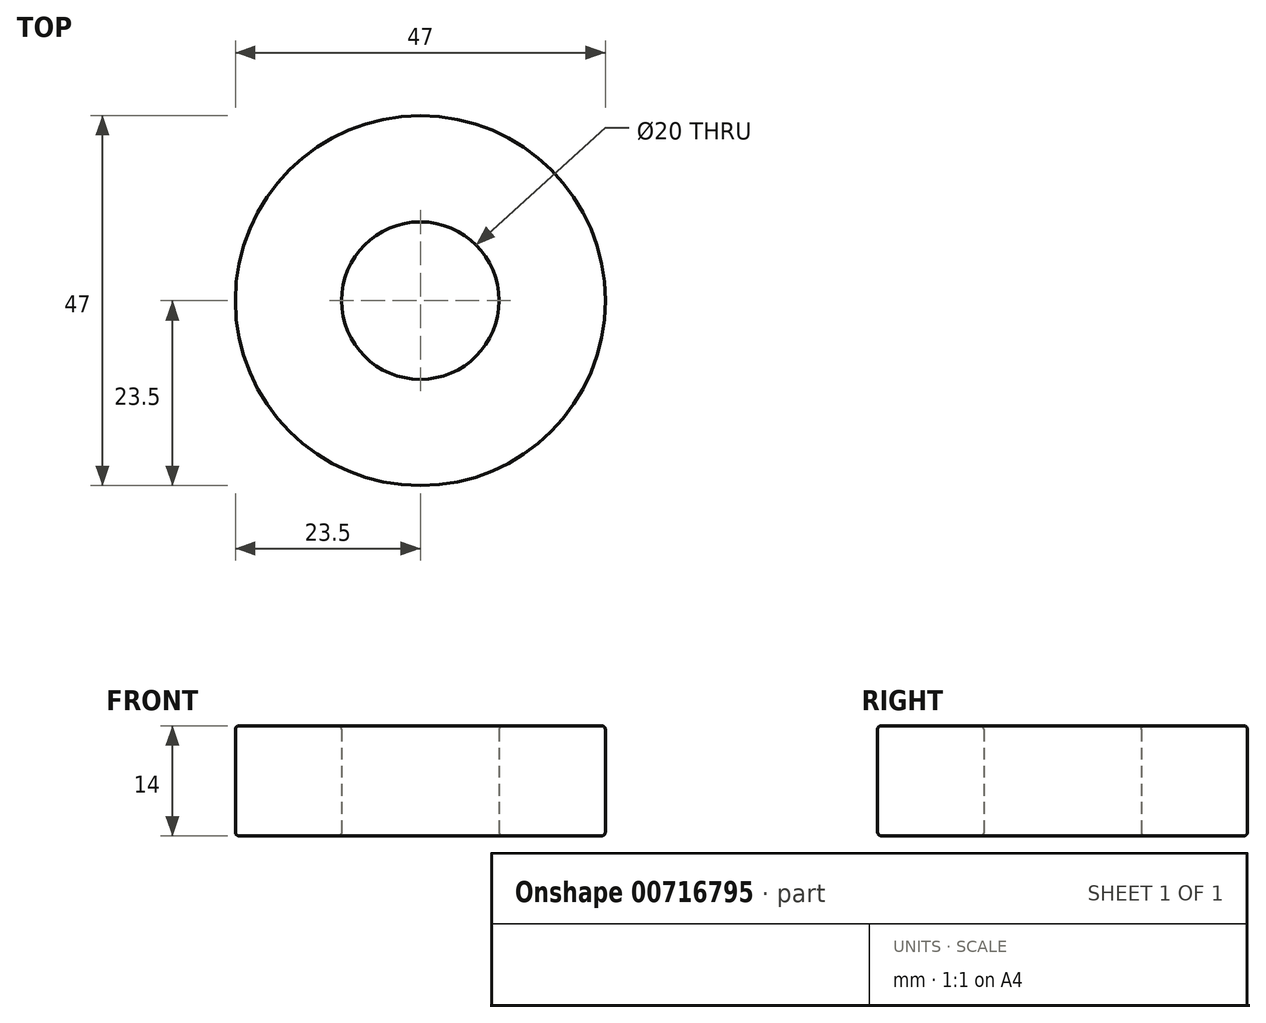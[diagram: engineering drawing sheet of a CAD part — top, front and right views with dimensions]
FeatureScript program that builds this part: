
annotation { "Feature Type Name" : "Feature", "Feature Type Description" : "" }
export const myFeature = defineFeature(function(context is Context, id is Id, definition is map)
    precondition{}
    {
        {
            var Q0;
            Q0=qCreatedBy(makeId("Top.planeOp"),FACE);
            var sketch = newSketch(context, id + "F0", { "sketchPlane" : qUnion([Q0])});
            skCircle(sketch, "E0", {"center": v(0, 0) * mm, "radius": 23.5 * mm});
            skCircle(sketch, "E1", {"center": v(0, 0) * mm, "radius": 10 * mm});
            skSolve(sketch);
        }
        {
            var Q0;
            Q0 = qSketchRegion(id + "F0", true);
            extrude(context, id + "F1", {"entities" : qUnion([Q0]), "endBound" : BoundingType.SYMMETRIC, "depth" : 14 * mm, "offsetDistance" : 25 * mm});
        }
        {
            var Q0;
            Q0=makeQuery(id+"F1.opExtrude","SWEPT_FACE",FACE,{"disambiguationData":[OSD([sQuery(id+"F0.wireOp",EDGE,"E0")])]});
            var Q1;
            Q1=makeQuery(id+"F1.opExtrude","SWEPT_FACE",FACE,{"disambiguationData":[OSD([sQuery(id+"F0.wireOp",EDGE,"E1")])]});
            fillet(context, id + "F2", {"entities" : qUnion([Q0, Q1]), "radius" : 0.5 * mm, "tangentPropagation" : true, "allowEdgeOverflow" : false});
        }
    });
